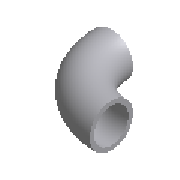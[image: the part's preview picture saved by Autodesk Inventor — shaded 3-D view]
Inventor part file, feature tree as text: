
AUTODESK INVENTOR PART (.ipt)
format: ipt  version: 2025.3 (Build 293356030, 356C)  size: 184,320 bytes
history: native  units: mm (DEFAULTED — no unit token found)
features: other x4, sweep x1
ambient origin geometry x8: Origin, YZ Plane, XZ Plane, XY Plane, X Axis, Y Axis, Z Axis, Center Point
bodies: Solid1 (feature_tree)
feature tree (5):
  sweep  "Sweep1"
  other  "Work Point1"
  other  "Work Point2"
  other  "Work Axis1"
  other  "Work Axis2"
